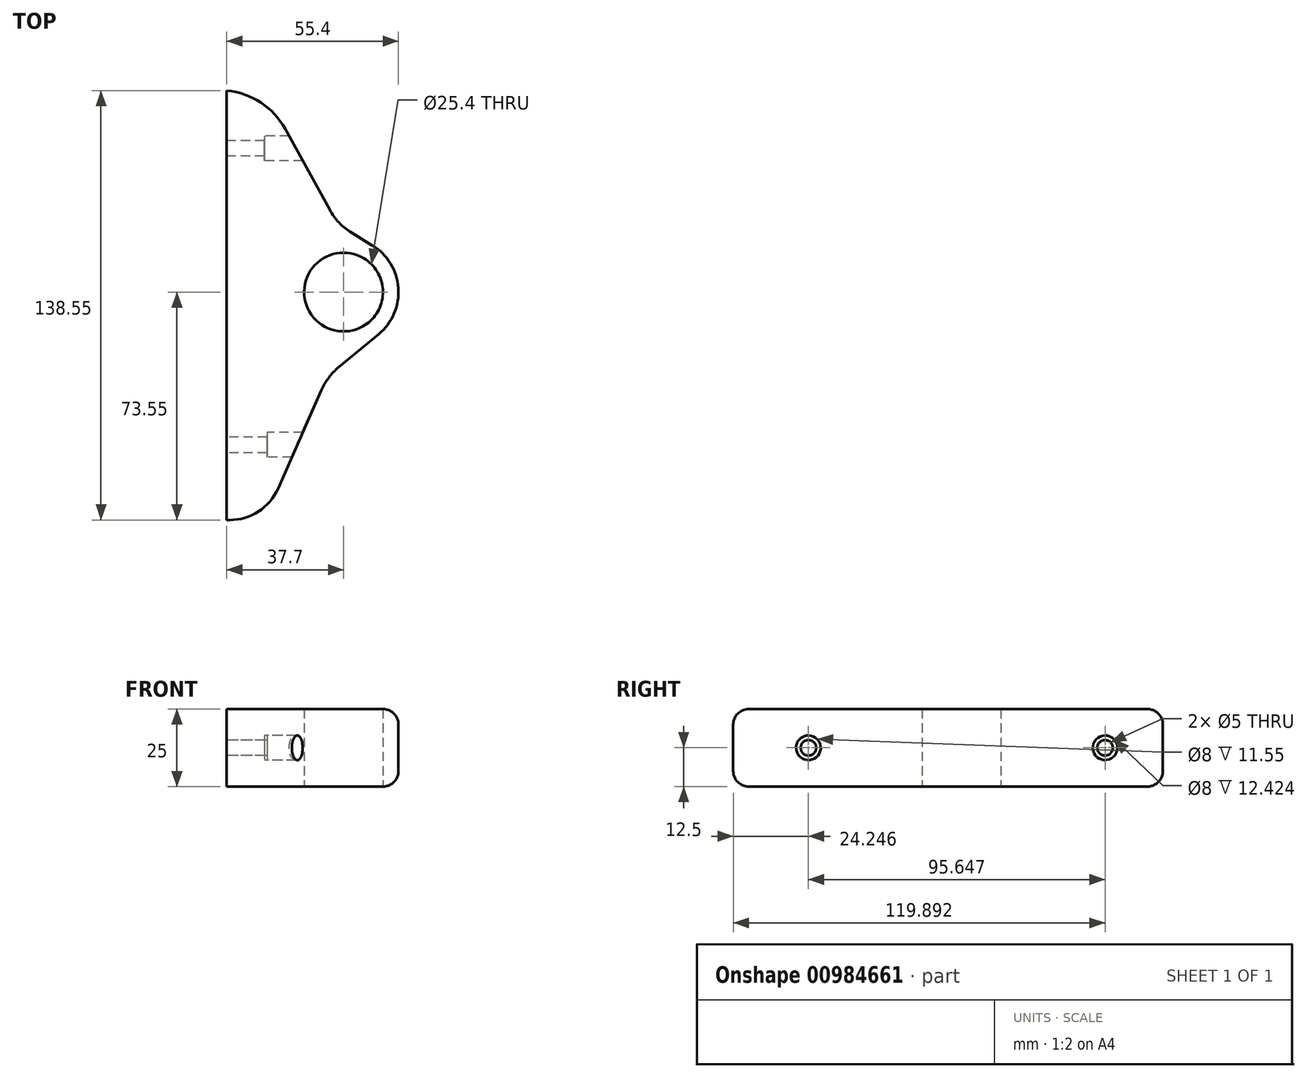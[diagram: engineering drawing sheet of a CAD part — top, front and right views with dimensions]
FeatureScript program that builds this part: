
annotation { "Feature Type Name" : "Feature", "Feature Type Description" : "" }
export const myFeature = defineFeature(function(context is Context, id is Id, definition is map)
    precondition{}
    {
        {
            var Q0;
            Q0=qCreatedBy(makeId("Top.planeOp"),FACE);
            var sketch = newSketch(context, id + "F0", { "sketchPlane" : qUnion([Q0])});
            skCircle(sketch, "E0", {"center": v(37.7, 0) * mm, "radius": 12.7 * mm});
            skLineSegment(sketch, "E1.bottom", {"start": v(0, 65) * mm, "end": v(12.09, 65) * mm});
            skLineSegment(sketch, "E1.top", {"start": v(0, -73.55) * mm, "end": v(12.09, -73.55) * mm});
            skLineSegment(sketch, "E1.left", {"start": v(0, 65) * mm, "end": v(0, -73.55) * mm});
            skArc(sketch, "E2", {"start": v(48.97, -13.65) * mm, "mid": v(55.35, 1.28) * mm, "end": v(46.9, 15.13) * mm});
            skLineSegment(sketch, "E3", {"start": v(12.09, -73.55) * mm, "end": v(30.58, -31.6) * mm});
            skLineSegment(sketch, "E4", {"start": v(36.15, -24.24) * mm, "end": v(48.97, -13.65) * mm});
            skLineSegment(sketch, "E5", {"start": v(12.09, -73.55) * mm, "end": v(12.09, 45.88) * mm, "construction": true});
            skLineSegment(sketch, "E6", {"start": v(12.09, 65) * mm, "end": v(33.2, 26.57) * mm});
            skLineSegment(sketch, "E7", {"start": v(40.34, 19.1) * mm, "end": v(46.9, 15.13) * mm});
            skPoint(sketch, "E8.visualSharp", {"position": v(35.77, 21.89) * mm});
            skArc(sketch, "E8.filletArc", {"start": v(33.2, 26.57) * mm, "mid": v(36.27, 22.37) * mm, "end": v(40.34, 19.1) * mm});
            skPoint(sketch, "E9.visualSharp", {"position": v(32.5, -27.25) * mm});
            skArc(sketch, "E9.filletArc", {"start": v(36.15, -24.24) * mm, "mid": v(32.94, -27.59) * mm, "end": v(30.58, -31.6) * mm});
            skSolve(sketch);
        }
        {
            var Q0;
            Q0=makeQuery(id+"F0.imprint","IMPRINT",FACE,{"disambiguationData":[TD([[makeQuery(id+"F0.imprint","IMPRINT",EDGE,{"derivedFrom":sQuery(id+"F0.wireOp",EDGE,"E0")}),-1.0]])]});
            extrude(context, id + "F1", {"entities" : qUnion([Q0]), "depth" : 25 * mm, "offsetDistance" : 25 * mm});
        }
        {
            var Q0;
            Q0=makeQuery(id+"F1.opExtrude","SWEPT_EDGE",EDGE,{"disambiguationData":[OSD([sQuery(id+"F0.wireOp",EDGE,"E1.top"),sQuery(id+"F0.wireOp",EDGE,"E3")])]});
            fillet(context, id + "F2", {"entities" : qUnion([Q0]), "radius" : 17 * mm, "tangentPropagation" : true, "allowEdgeOverflow" : false});
        }
        {
            var Q0;
            Q0=makeQuery(id+"F1.opExtrude","SWEPT_EDGE",EDGE,{"disambiguationData":[OSD([sQuery(id+"F0.wireOp",EDGE,"E1.bottom"),sQuery(id+"F0.wireOp",EDGE,"E6")])]});
            fillet(context, id + "F3", {"entities" : qUnion([Q0]), "radius" : 24.08 * mm, "tangentPropagation" : true, "allowEdgeOverflow" : false});
        }
        {
            var Q0;
            {var subQ0=sQuery(id+"F0.wireOp",EDGE,"E6");var subQ1=sQuery(id+"F0.wireOp",EDGE,"E1.bottom");Q0=makeQuery(id+"F3.opFillet","BLEND_EDGE",EDGE,{"blendedFrom":[makeQuery(id+"F1.opExtrude","SWEPT_EDGE",EDGE,{"disambiguationData":[OSD([subQ1,subQ0])]}),makeQuery(id+"F1.opExtrude","CAP_FACE",FACE,{"disambiguationData":[OSD([sQuery(id+"F0.wireOp",EDGE,"E0"),subQ1,sQuery(id+"F0.wireOp",EDGE,"E1.top"),sQuery(id+"F0.wireOp",EDGE,"E1.left"),sQuery(id+"F0.wireOp",EDGE,"E2"),sQuery(id+"F0.wireOp",EDGE,"E3"),sQuery(id+"F0.wireOp",EDGE,"E4"),subQ0,sQuery(id+"F0.wireOp",EDGE,"E7"),sQuery(id+"F0.wireOp",EDGE,"E8.filletArc"),sQuery(id+"F0.wireOp",EDGE,"E9.filletArc")])],"isStart":false})],"blendedInto":[makeQuery(id+"F1.opExtrude","CAP_FACE",FACE,{"disambiguationData":[OSD([sQuery(id+"F0.wireOp",EDGE,"E0"),subQ1,sQuery(id+"F0.wireOp",EDGE,"E1.top"),sQuery(id+"F0.wireOp",EDGE,"E1.left"),sQuery(id+"F0.wireOp",EDGE,"E2"),sQuery(id+"F0.wireOp",EDGE,"E3"),sQuery(id+"F0.wireOp",EDGE,"E4"),subQ0,sQuery(id+"F0.wireOp",EDGE,"E7"),sQuery(id+"F0.wireOp",EDGE,"E8.filletArc"),sQuery(id+"F0.wireOp",EDGE,"E9.filletArc")])],"isStart":false})]});}
            var Q1;
            {var subQ0=sQuery(id+"F0.wireOp",EDGE,"E6");var subQ1=sQuery(id+"F0.wireOp",EDGE,"E1.bottom");Q1=makeQuery(id+"F3.opFillet","BLEND_EDGE",EDGE,{"blendedFrom":[makeQuery(id+"F1.opExtrude","SWEPT_EDGE",EDGE,{"disambiguationData":[OSD([subQ1,subQ0])]}),makeQuery(id+"F1.opExtrude","CAP_FACE",FACE,{"disambiguationData":[OSD([sQuery(id+"F0.wireOp",EDGE,"E0"),subQ1,sQuery(id+"F0.wireOp",EDGE,"E1.top"),sQuery(id+"F0.wireOp",EDGE,"E1.left"),sQuery(id+"F0.wireOp",EDGE,"E2"),sQuery(id+"F0.wireOp",EDGE,"E3"),sQuery(id+"F0.wireOp",EDGE,"E4"),subQ0,sQuery(id+"F0.wireOp",EDGE,"E7"),sQuery(id+"F0.wireOp",EDGE,"E8.filletArc"),sQuery(id+"F0.wireOp",EDGE,"E9.filletArc")])],"isStart":true})],"blendedInto":[makeQuery(id+"F1.opExtrude","CAP_FACE",FACE,{"disambiguationData":[OSD([sQuery(id+"F0.wireOp",EDGE,"E0"),subQ1,sQuery(id+"F0.wireOp",EDGE,"E1.top"),sQuery(id+"F0.wireOp",EDGE,"E1.left"),sQuery(id+"F0.wireOp",EDGE,"E2"),sQuery(id+"F0.wireOp",EDGE,"E3"),sQuery(id+"F0.wireOp",EDGE,"E4"),subQ0,sQuery(id+"F0.wireOp",EDGE,"E7"),sQuery(id+"F0.wireOp",EDGE,"E8.filletArc"),sQuery(id+"F0.wireOp",EDGE,"E9.filletArc")])],"isStart":true})]});}
            fillet(context, id + "F4", {"entities" : qUnion([Q0, Q1]), "radius" : 5 * mm, "tangentPropagation" : true, "allowEdgeOverflow" : false});
        }
        {
            var Q0;
            Q0=qCreatedBy(makeId("Right.planeOp"),FACE);
            cPlane(context, id + "F5", {"entities" : qUnion([Q0]), "cplaneType" : CPlaneType.OFFSET, "offset" : 30 * mm, "width" : 150 * mm, "height" : 150 * mm});
        }
        {
            var Q0;
            Q0=qCreatedBy(id+"F5.planeOp",FACE);
            var sketch = newSketch(context, id + "F6", { "sketchPlane" : qUnion([Q0])});
            skLineSegment(sketch, "E10", {"start": v(57.07, 12.5) * mm, "end": v(-55.34, 12.5) * mm, "construction": true});
            skPoint(sketch, "E11", {"position": v(46.34, 12.5) * mm});
            skPoint(sketch, "E12", {"position": v(-49.3, 12.5) * mm});
            skSolve(sketch);
        }
        {
            var Q0;
            Q0=sQuery(id+"F6.wireOp",VERTEX,"E12");
            var Q1;
            Q1=sQuery(id+"F6.wireOp",VERTEX,"E11");
            var Q2;
            Q2=makeQuery(id+"F1.opExtrude","SWEPT_BODY",BODY,{"disambiguationData":[OSD([sQuery(id+"F0.wireOp",EDGE,"E0"),sQuery(id+"F0.wireOp",EDGE,"E1.bottom"),sQuery(id+"F0.wireOp",EDGE,"E1.top"),sQuery(id+"F0.wireOp",EDGE,"E1.left"),sQuery(id+"F0.wireOp",EDGE,"E2"),sQuery(id+"F0.wireOp",EDGE,"E3"),sQuery(id+"F0.wireOp",EDGE,"E4"),sQuery(id+"F0.wireOp",EDGE,"E6"),sQuery(id+"F0.wireOp",EDGE,"E7"),sQuery(id+"F0.wireOp",EDGE,"E8.filletArc"),sQuery(id+"F0.wireOp",EDGE,"E9.filletArc")])]});
            hole(context, id + "F7", {"style" : HoleStyle.C_BORE, "endStyle" : HoleEndStyle.THROUGH, "holeDiameter" : 5 * mm, "cBoreDiameter" : 8 * mm, "cBoreDepth" : 8 * mm, "majorDiameter" : 5 * mm, "isTappedThrough" : true, "tappedDepth" : 12 * mm, "tapClearance" : 3, "locations" : qUnion([Q0, Q1]), "scope" : qUnion([Q2]), "startStyle" : HoleStartStyle.PART});
        }
    });
